# Revit family: Practibox_S_22_modules_encastré_réf_137005_à_137175
name_source: partatom
category: Equipement électrique
revit_build: Autodesk Revit 2018 (Build: 20170223_1515(x64)
units: mm (PartAtom-declared; Revit-internal decimal feet)

## family parameters
Basée sur le plan de construction = Non
Configuration du panneau = Deux colonnes, circuits au sein
Cote de connecteur circulaire = Utiliser le diamètre
Couper avec des vides une fois chargée = Non
Numéro OmniClass = 23.80.30.11.17
Partagée = Non
Point de calcul de pièce = Non
Titre OmniClass = Distribution Boards and Control Panels
Toujours verticalement = Oui
Type d'élément = Tableau de raccordement

## types (8) — shared parameters
Conditions Générale d'Utilisation = https://export.legrand.com
Fabricant = "Legrand"
Hauteur = 235 mm  [stored 0.770997 ft]
Ina = 90 A
Largeur = 508 mm
URL = www.legrand.com
profondeur = 102 mm
taille = 22 modules

## per-type parameters (varying)
| type | Bornier N | Bornier T | porte blanche | porte transparente |
| Practibox_S_22_modules_encastré_137005 |  |  | Oui | Non |
| Practibox_S_22_modules_encastré_137015 |  |  | Non | Oui |
| Practibox_S_22_modules_encastré_137155 | 13 départs Icc 10kA | 13 départs Icc 10kA | Non | Oui |
| Practibox_S_22_modules_encastré_137145 | 13 départs Icc 10kA | 13 départs Icc 10kA | Oui | Non |
| Practibox_S_22_modules_encastré_137175 | 13 départs Icc 10kA | 13 départs Icc 10kA | Non | Oui |
| Practibox_S_22_modules_encastré_137025 |  |  | Oui | Non |
| Practibox_S_22_modules_encastré_137035 |  |  | Non | Oui |
| Practibox_S_22_modules_encastré_137165 | 13 départs Icc 10kA | 13 départs Icc 10kA | Oui | Non |

note: column(s) folded — value = type name in every type: Description

note: [stored X ft] marks values corroborated as IEEE doubles in the binary element streams (Revit-internal decimal feet)
